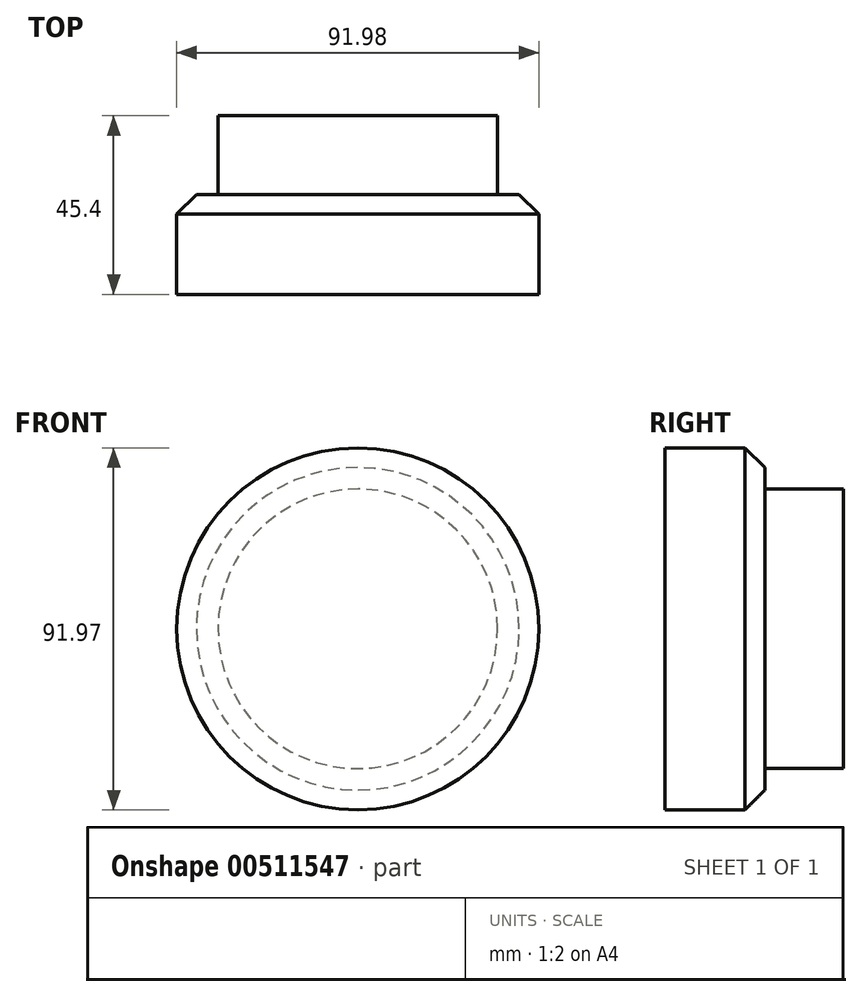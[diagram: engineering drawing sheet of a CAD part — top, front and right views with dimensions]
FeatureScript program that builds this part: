
annotation { "Feature Type Name" : "Feature", "Feature Type Description" : "" }
export const myFeature = defineFeature(function(context is Context, id is Id, definition is map)
    precondition{}
    {
        {
            var Q0;
            Q0=qCreatedBy(makeId("Front.planeOp"),FACE);
            var sketch = newSketch(context, id + "F0", { "sketchPlane" : qUnion([Q0])});
            skCircle(sketch, "E0", {"center": v(0, 5.38) * mm, "radius": 45.99 * mm});
            skSolve(sketch);
        }
        {
            var Q0;
            Q0=makeQuery(id+"F0.imprint","IMPRINT",FACE,{"disambiguationData":[TD([[makeQuery(id+"F0.imprint","IMPRINT",EDGE,{"derivedFrom":sQuery(id+"F0.wireOp",EDGE,"E0")}),1.0]])]});
            extrude(context, id + "F1", {"entities" : qUnion([Q0]), "endBound" : BoundingType.SYMMETRIC, "depth" : 25.4 * mm});
        }
        {
            var Q0;
            Q0=makeQuery(id+"F1.opExtrude","CAP_FACE",FACE,{"disambiguationData":[OSD([sQuery(id+"F0.wireOp",EDGE,"E0")])],"isStart":false});
            var sketch = newSketch(context, id + "F2", { "sketchPlane" : qUnion([Q0])});
            skLineSegment(sketch, "E1.bottom", {"start": v(0, 5.38) * mm, "end": v(27.15, 5.38) * mm});
            skLineSegment(sketch, "E1.top", {"start": v(0, 0) * mm, "end": v(27.15, 0) * mm});
            skLineSegment(sketch, "E1.left", {"start": v(0, 5.38) * mm, "end": v(0, 0) * mm, "construction": true});
            skLineSegment(sketch, "E1.right", {"start": v(27.15, 5.38) * mm, "end": v(27.15, 0) * mm, "construction": true});
            skSolve(sketch);
        }
        {
            var Q0;
            Q0=sQuery(id+"F2.wireOp",EDGE,"E1.bottom");
            var Q1;
            Q1=sQuery(id+"F2.wireOp",EDGE,"E1.top");
            extrude(context, id + "F3", {"bodyType" : ToolBodyType.SURFACE, "surfaceEntities" : qUnion([Q0, Q1]), "depth" : 25 * mm, "offsetDistance" : 25 * mm});
        }
        {
            var Q0;
            Q0=makeQuery(id+"F1.opExtrude","CAP_FACE",FACE,{"disambiguationData":[OSD([sQuery(id+"F0.wireOp",EDGE,"E0")])],"isStart":true});
            var sketch = newSketch(context, id + "F4", { "sketchPlane" : qUnion([Q0])});
            skCircle(sketch, "E2", {"center": v(0, 5.38) * mm, "radius": 35.51 * mm});
            skSolve(sketch);
        }
        {
            var Q0;
            Q0=makeQuery(id+"F4.imprint","IMPRINT",FACE,{"disambiguationData":[TD([[makeQuery(id+"F4.imprint","IMPRINT",EDGE,{"derivedFrom":sQuery(id+"F4.wireOp",EDGE,"E2")}),1.0]])]});
            extrude(context, id + "F5", {"entities" : qUnion([Q0]), "operationType" : NewBodyOperationType.ADD, "depth" : 20 * mm, "offsetDistance" : 25 * mm});
        }
        {
            var Q0;
            Q0=makeQuery(id+"F1.opExtrude","CAP_EDGE",EDGE,{"disambiguationData":[OSD([sQuery(id+"F0.wireOp",EDGE,"E0")])],"isStart":true});
            chamfer(context, id + "F6", {"entities" : qUnion([Q0]), "width" : 5 * mm, "tangentPropagation" : true});
        }
    });
